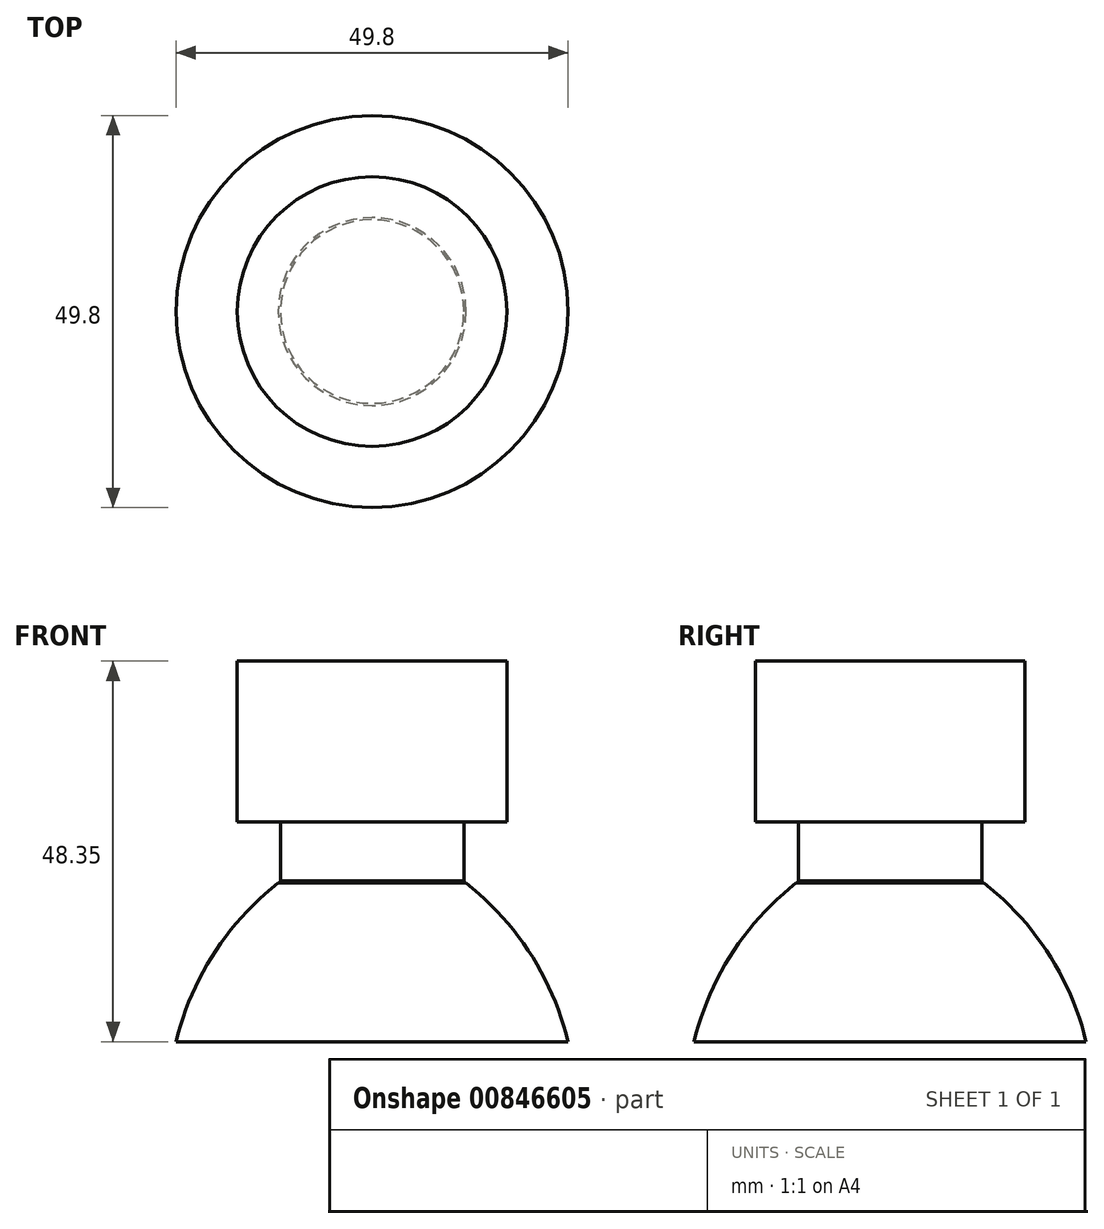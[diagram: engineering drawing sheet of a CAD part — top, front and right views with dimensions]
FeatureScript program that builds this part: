
annotation { "Feature Type Name" : "Feature", "Feature Type Description" : "" }
export const myFeature = defineFeature(function(context is Context, id is Id, definition is map)
    precondition{}
    {
        {
            var Q0;
            Q0=qCreatedBy(makeId("Front.planeOp"),FACE);
            var sketch = newSketch(context, id + "F0", { "sketchPlane" : qUnion([Q0])});
            skLineSegment(sketch, "E0", {"start": v(0, 41.59) * mm, "end": v(-16.84, 41.59) * mm});
            skLineSegment(sketch, "E1", {"start": v(-16.84, 41.59) * mm, "end": v(-16.84, 21.44) * mm});
            skLineSegment(sketch, "E2", {"start": v(-16.84, 21.44) * mm, "end": v(-11.94, 21.44) * mm});
            skLineSegment(sketch, "E3", {"start": v(-11.94, 21.44) * mm, "end": v(-11.94, 13.38) * mm});
            skLineSegment(sketch, "E4", {"start": v(-11.94, 13.38) * mm, "end": v(0, 13.38) * mm});
            skLineSegment(sketch, "E5", {"start": v(0, 13.38) * mm, "end": v(0, -6.76) * mm});
            skLineSegment(sketch, "E6", {"start": v(0, -6.76) * mm, "end": v(-24.9, -6.76) * mm});
            skLineSegment(sketch, "E7", {"start": v(-24.9, -6.76) * mm, "end": v(-11.94, 13.38) * mm});
            skArc(sketch, "E8", {"start": v(-11.94, 13.38) * mm, "mid": v(-20.12, 4.4) * mm, "end": v(-24.9, -6.76) * mm});
            skSolve(sketch);
        }
        {
            var Q0;
            Q0=qCreatedBy(makeId("Front.planeOp"),FACE);
            var sketch = newSketch(context, id + "F1", { "sketchPlane" : qUnion([Q0])});
            skLineSegment(sketch, "E9", {"start": v(0, 41.59) * mm, "end": v(0, 13.67) * mm});
            skLineSegment(sketch, "E10", {"start": v(0, 13.67) * mm, "end": v(-11.66, 13.67) * mm});
            skLineSegment(sketch, "E11", {"start": v(-11.66, 13.67) * mm, "end": v(-11.66, 21.15) * mm});
            skLineSegment(sketch, "E12", {"start": v(-11.66, 21.15) * mm, "end": v(-17.12, 21.15) * mm});
            skLineSegment(sketch, "E13", {"start": v(-17.12, 21.15) * mm, "end": v(-17.12, 41.59) * mm});
            skLineSegment(sketch, "E14", {"start": v(-17.12, 41.59) * mm, "end": v(0, 41.59) * mm});
            skSolve(sketch);
        }
        {
            var Q0;
            Q0=makeQuery(id+"F0.imprint","IMPRINT",FACE,{"disambiguationData":[TD([[makeQuery(id+"F0.imprint","IMPRINT",EDGE,{"derivedFrom":sQuery(id+"F0.wireOp",EDGE,"E7")}),1.0]])]});
            var Q1;
            Q1=makeQuery(id+"F0.imprint","IMPRINT",FACE,{"disambiguationData":[TD([[makeQuery(id+"F0.imprint","IMPRINT",EDGE,{"derivedFrom":sQuery(id+"F0.wireOp",EDGE,"E4")}),-1.0]])]});
            var Q2;
            Q2=makeQuery(id+"F1.imprint","IMPRINT",FACE,{"disambiguationData":[TD([[makeQuery(id+"F1.imprint","IMPRINT",EDGE,{"derivedFrom":sQuery(id+"F1.wireOp",EDGE,"E9")}),-1.0]])]});
            var Q3;
            Q3=sQuery(id+"F1.wireOp",EDGE,"E9");
            revolve(context, id + "F2", {"surfaceOperationType" : NewSurfaceOperationType.NEW, "entities" : qUnion([Q0, Q1, Q2]), "axis" : qUnion([Q3]), "revolveType" : RevolveType.FULL});
        }
    });
